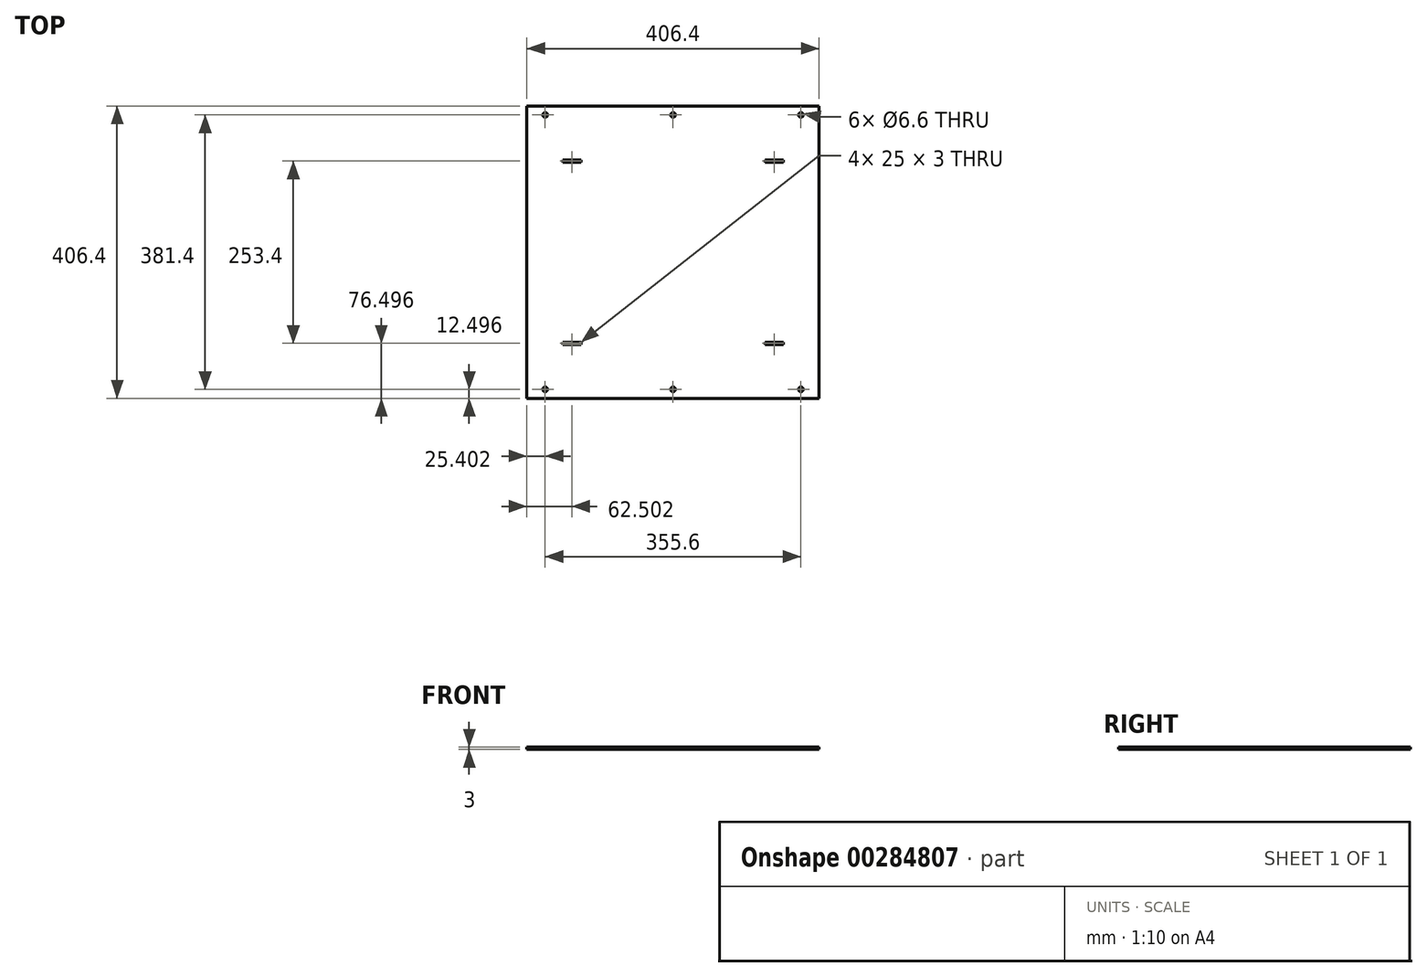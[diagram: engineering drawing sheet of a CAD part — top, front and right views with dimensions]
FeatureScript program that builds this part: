
annotation { "Feature Type Name" : "Feature", "Feature Type Description" : "" }
export const myFeature = defineFeature(function(context is Context, id is Id, definition is map)
    precondition{}
    {
        {
            var Q0;
            Q0=qCreatedBy(makeId("Top.planeOp"),FACE);
            var sketch = newSketch(context, id + "F0", { "sketchPlane" : qUnion([Q0])});
            skLineSegment(sketch, "E0.bottom", {"start": v(-241.68, 210.35) * mm, "end": v(164.72, 210.35) * mm});
            skLineSegment(sketch, "E0.top", {"start": v(-241.68, -196.05) * mm, "end": v(164.72, -196.05) * mm});
            skLineSegment(sketch, "E0.left", {"start": v(-241.68, 210.35) * mm, "end": v(-241.68, -196.05) * mm});
            skLineSegment(sketch, "E0.right", {"start": v(164.72, 210.35) * mm, "end": v(164.72, -196.05) * mm});
            skSolve(sketch);
        }
        {
            var Q0;
            Q0 = qSketchRegion(id + "F0", true);
            extrude(context, id + "F1", {"entities" : qUnion([Q0]), "depth" : 3 * mm});
        }
        {
            var Q0;
            Q0=makeQuery(id+"F1.opExtrude","CAP_FACE",FACE,{"disambiguationData":[OSD([sQuery(id+"F0.wireOp",EDGE,"E0.bottom"),sQuery(id+"F0.wireOp",EDGE,"E0.top"),sQuery(id+"F0.wireOp",EDGE,"E0.left"),sQuery(id+"F0.wireOp",EDGE,"E0.right")])],"isStart":false});
            var sketch = newSketch(context, id + "F2", { "sketchPlane" : qUnion([Q0])});
            skPoint(sketch, "E1", {"position": v(-216.28, 197.85) * mm});
            skPoint(sketch, "E2", {"position": v(-38.48, 197.85) * mm});
            skPoint(sketch, "E3", {"position": v(139.32, 197.85) * mm});
            skPoint(sketch, "E4", {"position": v(139.32, -183.55) * mm});
            skPoint(sketch, "E5", {"position": v(-38.48, -183.55) * mm});
            skPoint(sketch, "E6", {"position": v(-216.28, -183.55) * mm});
            skSolve(sketch);
        }
        {
            var Q0;
            Q0=sQuery(id+"F2.wireOp",VERTEX,"E1");
            var Q1;
            Q1=sQuery(id+"F2.wireOp",VERTEX,"E2");
            var Q2;
            Q2=sQuery(id+"F2.wireOp",VERTEX,"E3");
            var Q3;
            Q3=sQuery(id+"F2.wireOp",VERTEX,"E4");
            var Q4;
            Q4=sQuery(id+"F2.wireOp",VERTEX,"E5");
            var Q5;
            Q5=sQuery(id+"F2.wireOp",VERTEX,"E6");
            var Q6;
            Q6=makeQuery(id+"F1.opExtrude","SWEPT_BODY",BODY,{"disambiguationData":[OSD([sQuery(id+"F0.wireOp",EDGE,"E0.bottom"),sQuery(id+"F0.wireOp",EDGE,"E0.top"),sQuery(id+"F0.wireOp",EDGE,"E0.left"),sQuery(id+"F0.wireOp",EDGE,"E0.right")])]});
            hole(context, id + "F3", {"style" : HoleStyle.SIMPLE, "endStyle" : HoleEndStyle.THROUGH, "standardTappedOrClearance" : lookupTablePath({ "standard" : "ISO", "fit" : "Normal", "size" : "M6", "type" : "Clearance" }), "standardBlindInLast" : lookupTablePath({ "fit" : "Standard", "standard" : "ISO", "size" : "M6", "type" : "Clearance" }), "holeDiameter" : 6.6 * mm, "tappedDepth" : 12 * mm, "tapClearance" : 3, "locations" : qUnion([Q0, Q1, Q2, Q3, Q4, Q5]), "scope" : qUnion([Q6])});
        }
        {
            var Q0;
            Q0=makeQuery(id+"F1.opExtrude","CAP_FACE",FACE,{"disambiguationData":[OSD([sQuery(id+"F0.wireOp",EDGE,"E0.bottom"),sQuery(id+"F0.wireOp",EDGE,"E0.top"),sQuery(id+"F0.wireOp",EDGE,"E0.left"),sQuery(id+"F0.wireOp",EDGE,"E0.right")])],"isStart":false});
            var sketch = newSketch(context, id + "F4", { "sketchPlane" : qUnion([Q0])});
            skLineSegment(sketch, "E7.bottom", {"start": v(-191.68, 135.35) * mm, "end": v(-166.68, 135.35) * mm});
            skLineSegment(sketch, "E7.top", {"start": v(-191.68, 132.35) * mm, "end": v(-166.68, 132.35) * mm});
            skLineSegment(sketch, "E7.left", {"start": v(-191.68, 135.35) * mm, "end": v(-191.68, 132.35) * mm});
            skLineSegment(sketch, "E7.right", {"start": v(-166.68, 135.35) * mm, "end": v(-166.68, 132.35) * mm});
            skLineSegment(sketch, "E8.bottom", {"start": v(89.72, 135.35) * mm, "end": v(114.72, 135.35) * mm});
            skLineSegment(sketch, "E8.top", {"start": v(89.72, 132.35) * mm, "end": v(114.72, 132.35) * mm});
            skLineSegment(sketch, "E8.left", {"start": v(89.72, 135.35) * mm, "end": v(89.72, 132.35) * mm});
            skLineSegment(sketch, "E8.right", {"start": v(114.72, 135.35) * mm, "end": v(114.72, 132.35) * mm});
            skLineSegment(sketch, "E9.bottom", {"start": v(-191.68, -118.05) * mm, "end": v(-166.68, -118.05) * mm});
            skLineSegment(sketch, "E9.top", {"start": v(-191.68, -121.05) * mm, "end": v(-166.68, -121.05) * mm});
            skLineSegment(sketch, "E9.left", {"start": v(-191.68, -118.05) * mm, "end": v(-191.68, -121.05) * mm});
            skLineSegment(sketch, "E9.right", {"start": v(-166.68, -118.05) * mm, "end": v(-166.68, -121.05) * mm});
            skLineSegment(sketch, "E10.bottom", {"start": v(89.72, -118.05) * mm, "end": v(114.72, -118.05) * mm});
            skLineSegment(sketch, "E10.top", {"start": v(89.72, -121.05) * mm, "end": v(114.72, -121.05) * mm});
            skLineSegment(sketch, "E10.left", {"start": v(89.72, -118.05) * mm, "end": v(89.72, -121.05) * mm});
            skLineSegment(sketch, "E10.right", {"start": v(114.72, -118.05) * mm, "end": v(114.72, -121.05) * mm});
            skSolve(sketch);
        }
        {
            var Q0;
            Q0 = qSketchRegion(id + "F4", true);
            extrude(context, id + "F5", {"entities" : qUnion([Q0]), "operationType" : NewBodyOperationType.REMOVE, "oppositeDirection" : true, "depth" : 25 * mm, "offsetDistance" : 25 * mm});
        }
    });
